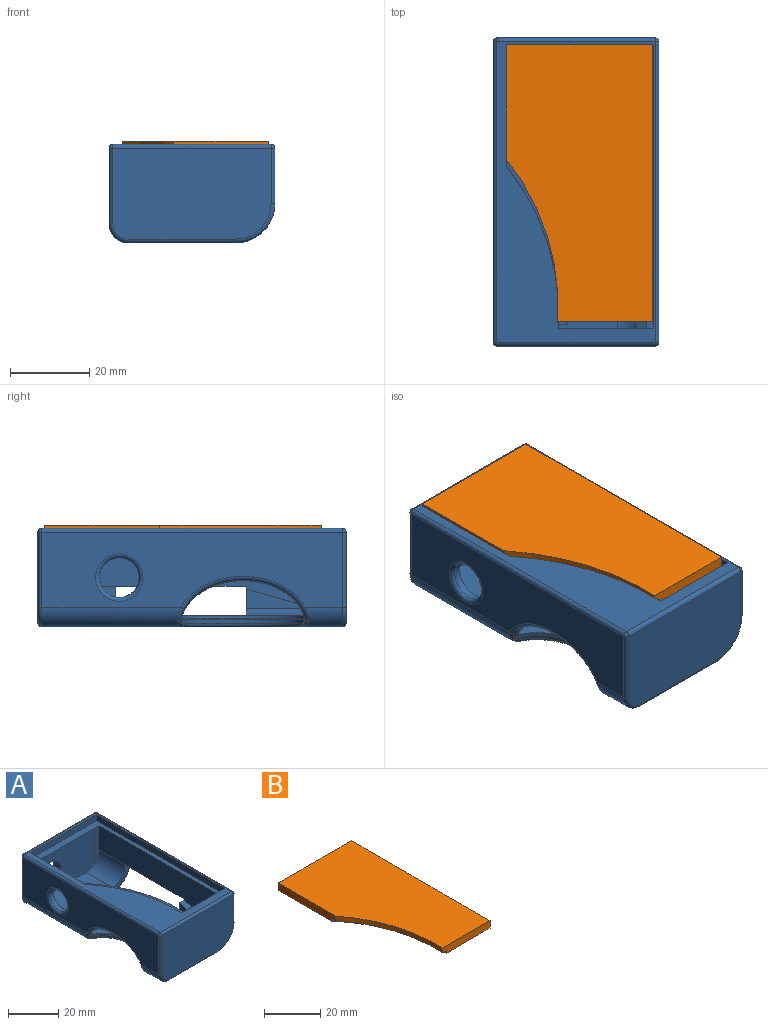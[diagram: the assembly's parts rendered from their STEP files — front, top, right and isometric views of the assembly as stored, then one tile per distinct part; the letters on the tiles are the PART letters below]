
ASSEMBLY  parts=2 mates=1
PART A: 110 faces, bbox 43.3x78x25.8 mm
  f0: plane 76x40mm, normal (0,0,1), area 771.2mm2, adj f9,f10,f30,f82,f90,f91,f94,f95
  f1: plane 2x1.1mm, normal (1,0,0), area 2.2mm2, adj f5,f25,f32,f107
  f2: plane 68.74x28.04mm, normal (0,0,1), area 1743.1mm2, adj f3,f15,f34,f42,f46,f50,f80,f103
  f3: cylinder r=1mm len=6.68mm, axis (0,-1,0), area 10.3mm2, adj f2,f34,f35,f36,f76,f108
  f4: plane 68.65x18.3mm, normal (-1,0,0), area 881.1mm2, adj f8,f17,f20,f45,f50,f83,f107
  f5: plane 1.4x1.1mm, normal (0,0,-1), area 1.5mm2, adj f1,f10,f32,f107
  f6: plane 0.54x0.52mm, normal (0,-1,0), area 0.3mm2, adj f9,f23,f24,f37
  f7: plane 17.22x0.09mm, normal (-1,0,0), area 0.9mm2, adj f8,f15,f50,f83
  f8: plane 17.23x2.4mm, normal (0,-1,0), area 37.3mm2, adj f4,f7,f50,f83
  f9: plane 30.67x3mm, normal (1,0,0), area 42.1mm2, adj f0,f6,f10,f15,f23,f24,f81,f83
  f10: cylinder r=59.56mm len=40.98mm, axis (0,0,1), area 52.8mm2, adj f0,f5,f9,f30,f81,f102
  f11: plane 2x1.8mm, normal (0,1,0), area 3.6mm2, adj f24,f25,f26,f37,f81
  f12: bspline ~3.96x2.14mm, area 4.6mm2, adj f13,f52,f55,f69
  f13: revolved ~31.34x9.84mm, area 36.4mm2, adj f12,f14,f55,f71
  f14: bspline ~4.38x2.09mm, area 4.6mm2, adj f13,f51,f55,f74
  f15: plane 33.57x20.48mm, normal (0,-1,0), area 563.4mm2, adj f2,f7,f9,f23,f25,f36,f37,f40
  f16: plane 33.04x0.03mm, normal (1,0,0), area 0.9mm2, adj f17,f19,f20,f49
  f17: plane 9.71x9.71mm, normal (0,1,0), area 36.1mm2, adj f4,f16,f18,f20,f41,f42,f45,f46
  f18: plane 17.68x4.99mm, normal (-1,0,0), area 44.1mm2, adj f17,f45,f46
  f19: plane 9.71x9.71mm, normal (0,-1,0), area 29mm2, adj f16,f20,f41,f42,f48,f49,f50,f58
  f20: cylinder r=10.76mm len=33.04mm, axis (0,-1,0), area 34.2mm2, adj f4,f16,f17,f19
  f21: plane 76x14mm, normal (1,0,0), area 1003.9mm2, adj f43,f44,f61,f63,f65,f86,f91,f96
  f22: plane 76x27.01mm, normal (0,0,-1), area 1813.7mm2, adj f43,f44,f51,f52,f56,f58,f60,f62
  f23: plane 0.54x0.1mm, normal (0,0,-1), area 0.1mm2, adj f6,f9,f15,f37
  f24: plane 25.69x0.54mm, normal (0,0,-1), area 13.9mm2, adj f6,f9,f11,f37
  f25: plane 68.72x16.06mm, normal (0,0,-1), area 518.7mm2, adj f1,f11,f15,f26,f32,f36,f37,f103
  f26: cylinder r=59mm len=41.8mm, axis (0,0,1), area 90.4mm2, adj f11,f25,f32,f81
  f27: plane 76x19mm, normal (-1,0,0), area 1152.7mm2, adj f51,f52,f53,f55,f89,f94,f99
  f28: plane 40x23mm, normal (0,-1,0), area 899.2mm2, adj f95,f96,f98,f99,f100,f101
  f29: plane 40x23mm, normal (0,1,0), area 519.1mm2, adj f38,f84,f85,f86,f87,f89,f90
  f30: plane 24x3mm, normal (0,1,0), area 32.5mm2, adj f0,f10,f82,f83,f102,f104,f105,f106
  f31: cylinder r=5mm len=10mm, axis (-1,0,0), area 56.5mm2, adj f36,f53
  f32: plane 3.6x2mm, normal (0,-1,0), area 7.2mm2, adj f1,f5,f25,f26,f81
  f33: revolved ~31.34x9.84mm, area 36.4mm2, adj f54,f56,f57,f70
  f34: extruded ~31.19x9.6mm, area 26.6mm2, adj f2,f3,f35,f70,f76,f80
  f35: extruded ~31.19x9.6mm, area 26.6mm2, adj f3,f34,f36,f71,f76,f80
  f36: plane 68.74x18.2mm, normal (1,0,0), area 990.5mm2, adj f3,f15,f25,f31,f35,f80,f108
  f37: plane 25.79x2mm, normal (1,0,0), area 51.5mm2, adj f6,f11,f15,f23,f24,f25
  f38: cylinder r=11mm len=22mm, axis (0,1,0), area 69.1mm2, adj f29,f39
  f39: plane 22x22mm, normal (0,1,0), area 301.6mm2, adj f38,f40
  f40: cylinder r=5mm len=10mm, axis (0,1,0), area 121.9mm2, adj f15,f39
  f41: cylinder r=10.76mm len=33.05mm, axis (0,-1,0), area 36.2mm2, adj f17,f19,f48,f61,f63,f65
  f42: cylinder r=10.76mm len=33.05mm, axis (0,-1,0), area 63.3mm2, adj f2,f17,f19,f58,f60,f62
  f43: cylinder r=10mm len=17.65mm, axis (0,1,0), area 277.2mm2, adj f21,f22,f59,f84
  f44: cylinder r=10mm len=23.31mm, axis (0,1,0), area 366.2mm2, adj f21,f22,f64,f98
  f45: plane 20.88x5.89mm, normal (0,-0.27,0.96), area 52.1mm2, adj f4,f17,f18,f47,f107
  f46: cylinder r=7.16mm len=20.88mm, axis (0,1,0), area 108.6mm2, adj f2,f17,f18,f47,f107
  f47: plane 3.2x0.9mm, normal (1,0,0), area 1.4mm2, adj f45,f46,f107
  f48: plane 33.04x0.02mm, normal (1,0,0), area 0.7mm2, adj f17,f19,f41,f49
  f49: plane 33.04x0.23mm, normal (0,0,-1), area 7.7mm2, adj f16,f17,f19,f48
  f50: cylinder r=7.47mm len=14.77mm, axis (0,-1,0), area 168.4mm2, adj f2,f4,f7,f8,f15,f19
  f51: cylinder r=5mm len=35.18mm, axis (0,-1,0), area 271.6mm2, adj f14,f22,f27,f57,f73,f75,f87
  f52: cylinder r=5mm len=9.38mm, axis (0,-1,0), area 69mm2, adj f12,f22,f27,f54,f66,f67,f101
  f53: torus R=6mm, axis (-1,0,0), area 52.9mm2, adj f27,f31
  f54: bspline ~4.38x2.09mm, area 4.6mm2, adj f33,f52,f56,f68
  f55: bspline ~32.68x9.59mm, area 52.7mm2, adj f12,f13,f14,f27
  f56: bspline ~32.68x9.59mm, area 52.7mm2, adj f22,f33,f54,f57
  f57: bspline ~3.96x2.14mm, area 4.6mm2, adj f33,f51,f56,f72
  f58: cylinder r=1mm len=1.71mm, axis (-1,0,0), area 1.7mm2, adj f19,f22,f42,f59,f60
  f59: torus R=9mm, axis (0,-1,0), area 23.8mm2, adj f19,f43,f58,f61
  f60: cylinder r=1mm len=35.04mm, axis (0,-1,0), area 50.6mm2, adj f22,f42,f58,f62
  f61: cylinder r=1mm len=1.71mm, axis (0,0,-1), area 1.7mm2, adj f19,f21,f41,f59,f63
  f62: cylinder r=1mm len=1.71mm, axis (1,0,0), area 1.7mm2, adj f17,f22,f42,f60,f64
  f63: cylinder r=1mm len=35.04mm, axis (0,-1,0), area 50.6mm2, adj f21,f41,f61,f65
  f64: torus R=9mm, axis (0,1,0), area 23.8mm2, adj f17,f44,f62,f65
  f65: cylinder r=1mm len=1.71mm, axis (0,0,1), area 1.7mm2, adj f17,f21,f41,f63,f64
  f66: bspline ~1.39x1.19mm, area 0mm2, adj f52,f68,f79
  f67: bspline ~1.93x1.7mm, area 0mm2, adj f52,f69,f79
  f68: sphere r=1mm, area 0.1mm2, adj f54,f66,f70,f78
  f69: sphere r=1mm, area 0.1mm2, adj f12,f67,f71,f78
  f70: bspline ~31.4x9.93mm, area 7.1mm2, adj f33,f34,f68,f71,f72,f77
  f71: bspline ~31.38x9.81mm, area 7.1mm2, adj f13,f35,f69,f70,f74,f77
  f72: sphere r=1mm, area 0.1mm2, adj f57,f70,f73,f74
  f73: bspline ~1.39x1.19mm, area 0mm2, adj f51,f72,f75
  f74: sphere r=1mm, area 0.1mm2, adj f14,f71,f72,f75
  f75: bspline ~1.93x1.7mm, area 0mm2, adj f51,f73,f74
  f76: bspline ~1.95x1.95mm, area 0.5mm2, adj f3,f34,f35,f77
  f77: bspline ~0.52x0.52mm, area 0.1mm2, adj f70,f71,f76,f78
  f78: torus R=1.82mm, axis (0.71,0,-0.71), area 0.1mm2, adj f68,f69,f77,f79
  f79: bspline ~0.54x0.15mm, area 0mm2, adj f66,f67,f78
  f80: cylinder r=0.82mm len=31.91mm, axis (0,-1,0), area 40.9mm2, adj f2,f15,f34,f35,f36
  f81: plane 41.8x15.37mm, normal (0,0,1), area 104.8mm2, adj f9,f10,f11,f26,f32
  f82: plane 71.65x3mm, normal (-1,0,0), area 215mm2, adj f0,f30,f83,f109
  f83: plane 71.65x37mm, normal (0,0,1), area 225.8mm2, adj f4,f7,f8,f9,f15,f30,f82,f106
  f84: torus R=9mm, axis (0,1,0), area 23.8mm2, adj f29,f43,f85,f86
  f85: cylinder r=1mm len=27mm, axis (-1,0,0), area 42.4mm2, adj f22,f29,f84,f87
  f86: cylinder r=1mm len=14mm, axis (0,0,1), area 22mm2, adj f21,f29,f84,f88
  f87: torus R=4mm, axis (0,1,0), area 11.4mm2, adj f29,f51,f85,f89
  f88: sphere r=1mm, area 1mm2, adj f86,f90,f91
  f89: cylinder r=1mm len=19mm, axis (0,0,-1), area 29.8mm2, adj f27,f29,f87,f92
  f90: cylinder r=1mm len=40mm, axis (1,0,0), area 62.8mm2, adj f0,f29,f88,f92
  f91: cylinder r=1mm len=76mm, axis (0,-1,0), area 119.4mm2, adj f0,f21,f88,f93
  f92: sphere r=1mm, area 2.1mm2, adj f89,f90,f94
  f93: sphere r=1mm, area 1.6mm2, adj f91,f95,f96
  f94: cylinder r=1mm len=76mm, axis (0,1,0), area 119.4mm2, adj f0,f27,f92,f97
  f95: cylinder r=1mm len=40mm, axis (-1,0,0), area 62.8mm2, adj f0,f28,f93,f97
  f96: cylinder r=1mm len=14mm, axis (0,0,-1), area 22mm2, adj f21,f28,f93,f98
  f97: sphere r=1mm, area 1.1mm2, adj f94,f95,f99
  f98: torus R=9mm, axis (0,1,0), area 23.8mm2, adj f28,f44,f96,f100
  f99: cylinder r=1mm len=19mm, axis (0,0,1), area 29.8mm2, adj f27,f28,f97,f101
  f100: cylinder r=1mm len=27mm, axis (1,0,0), area 42.4mm2, adj f22,f28,f98,f101
  f101: torus R=4mm, axis (0,1,0), area 11.4mm2, adj f28,f52,f99,f100
  f102: plane 21.08x0.07mm, normal (0,0,1), area 1.5mm2, adj f10,f30,f104,f107
  f103: plane 19x0.03mm, normal (-1,0,0), area 0.5mm2, adj f2,f25,f107,f108
  f104: plane 0.52x0.07mm, normal (1,0,0), area 0mm2, adj f30,f102,f105,f107
  f105: plane 1.2x0.07mm, normal (0,0,1), area 0.1mm2, adj f30,f104,f106,f107
  f106: plane 1.28x0.07mm, normal (1,0,0), area 0.1mm2, adj f30,f83,f105,f107
  f107: plane 23.61x21mm, normal (0,1,0), area 428mm2, adj f1,f2,f4,f5,f25,f45,f46,f47
  f108: plane 19x15.64mm, normal (0,1,0), area 296.9mm2, adj f2,f3,f25,f36,f103
  f109: plane 37x3mm, normal (0,-1,0), area 111mm2, adj f0,f9,f82,f83
PART B: 9 faces, bbox 37x70x3.2 mm
  f0: plane 24x3.2mm, normal (0,-1,0), area 74.6mm2, adj f1,f3,f4,f6,f7,f8
  f1: plane 70x37mm, normal (0,0,-1), area 2135.1mm2, adj f0,f2,f4,f5,f7
  f2: plane 29.02x3.2mm, normal (-1,0,0), area 90.3mm2, adj f1,f3,f5,f6,f7,f8
  f3: cylinder r=59.56mm len=40.98mm, axis (0,0,-1), area 88mm2, adj f0,f2,f6,f8
  f4: plane 70x3.2mm, normal (1,0,0), area 224mm2, adj f0,f1,f5,f6
  f5: plane 37x3.2mm, normal (0,1,0), area 118.4mm2, adj f1,f2,f4,f6
  f6: plane 70x37mm, normal (0,0,1), area 2207.7mm2, adj f0,f2,f3,f4,f5
  f7: cylinder r=61.01mm len=43.09mm, axis (0,0,-1), area 56mm2, adj f0,f1,f2,f8
  f8: plane 43.09x14.92mm, normal (0,0,-1), area 72.7mm2, adj f0,f2,f3,f7
PLACE A t=(-11.42,-4.55,23.12)mm
PLACE B t=(-11.56,-2.64,-23.58)mm
MATE fastened A.f81 <-> B.f8  axis (0,0,1) through (1.92,22.54,46.92)mm
